# Revit family: FA_Молниеприемник_EZETEK
name_source: partatom
category: Системы пожарной сигнализации
revit_build: Autodesk Revit 2017 (Build: 20170118_1100(x64)
units: mm (PartAtom-declared; Revit-internal decimal feet)

## family parameters
Всегда вертикально = Да
На основе рабочей плоскости = Нет
Общий = Нет
При загрузке вырезать с полостями = Нет
Размер круглого соединителя = Использовать радиус
Сохранять ориентацию аннотаций = Нет
Тип детали = Нормальный
Точка расчета площади = Нет

## types (17) — shared parameters
ADSK_Версия Revit = 2017
ADSK_Единица измерения = шт.
ADSK_Завод-изготовитель = Ezetek
ADSK_Количество = 1
URL = https://ezetek.ru
Группа модели = Молниеотводы и мачты на утяжелителях
Изготовитель = Ezetek
Описание = Молниеприемник

## per-type parameters (varying)
| type | ADSK_Код изделия | ADSK_Марка | ADSK_Масса | ADSK_Масса_Текст | ADSK_Материал | ADSK_Наименование | ADSK_Обозначение | ADSK_Размер_Диаметр | ADSK_Размер_Длина |
| Молниеприемник_1м_алюм_90870 | 90870 | 90870 | 0.6 | 0.6 | BIMLIB_Алюминий_EZETEK | Молниеприемник 1 м, алюм. | 90870 | 16 мм | 1000 мм |
| Молниеприемник_0.5м_алюм_90874-2 | 90874-2 | 90874-2 | 0.3 | 0.3 | BIMLIB_Алюминий_EZETEK | Молниеприемник 0.5 м, алюм. | 90874-2 | 16 мм | 500 мм |
| Молниеприемник_0,5м_алюм_76514 | 76514 | 76514 | 0.3 | 0.3 | BIMLIB_Алюминий_EZETEK | Молниеприемник 20 мм х 0.5 м, алюм. | 76514 | 20 мм | 500 мм |
| Молниеприемник_1м_нерж_90859 | 90859 | 90859 | 1.5 | 1.5 | BIMLIB_Сталь_Нержавеющая_EZETEK | Молниеприемник 1 м, нерж. | 90859 | 16 мм | 1000 мм |
| Молниеприемник_1.5м_алюм_90871 | 90871 | 90871 | 0.9 | 0.9 | BIMLIB_Алюминий_EZETEK | Молниеприемник 1.5 м, алюм. | 90871 | 16 мм | 1500 мм |
| Молниеприемник_0.5м_нерж_90370-1 | 90370-1 | 90370-1 | 0.75 | 0.75 | BIMLIB_Сталь_Нержавеющая_EZETEK | Молниеприемник 0.5 м, нерж. | 90370-1 | 16 мм | 500 мм |
| Молниеприемник_1.5м_нерж_90370 | 90370 | 90370 | 2.25 | 2.25 | BIMLIB_Сталь_Нержавеющая_EZETEK | Молниеприемник 1.5 м, нерж. | 90370 | 16 мм | 1500 мм |
| Молниеприемник_2м_алюм_90872 | 90872 | 90872 | 1.2 | 1.2 | BIMLIB_Алюминий_EZETEK | Молниеприемник 2 м, алюм. | 90872 | 16 мм | 2000 мм |
| Молниеприемник_2м_нерж_90371 | 90371 | 90371 | 3 | 3 | BIMLIB_Сталь_Нержавеющая_EZETEK | Молниеприемник 2 м, нерж. | 90371 | 16 мм | 2000 мм |
| Молниеприемник_2.5м_алюм_90874 | 90874 | 90874 | 1.4 | 1.4 | BIMLIB_Алюминий_EZETEK | Молниеприемник 2.5 м, алюм. | 90874 | 16 мм | 2500 мм |
| Молниеприемник_3м_алюм_23404 | 23404 | 23404 | 1.8 | 1.8 | BIMLIB_Алюминий_EZETEK | Молниеприемник 20 мм х 3 м, алюм. | 23404 | 20 мм | 3000 мм |
| Молниеприемник_3м_нерж_90858 | 90858 | 90858 | 4.5 | 4.5 | BIMLIB_Сталь_Нержавеющая_EZETEK | Молниеприемник 3 м, нерж. | 90858 | 16 мм | 3000 мм |
| Молниеприемник_4м_нерж_90372 | 90372 | 90372 | 6 | 6 | BIMLIB_Сталь_Нержавеющая_EZETEK | Молниеприемник 4 м, нерж. | 90372 | 16 мм | 4000 мм |
| Молниеприемник_1м_медь_90872-4 | 90872-4 | 90872-4 | 1.8 | 1.8 | BIMLIB_Медь_EZETEK | Молниеприемник 1 м, медь | 90872-4 | 16 мм | 1000 мм |
| Молниеприемник_1.5м_медь_90872-3 | 90872-3 | 90872-3 | 2.7 | 2.7 | BIMLIB_Медь_EZETEK | Молниеприемник 1,5 м, медь | 90872-3 | 16 мм | 1500 мм |
| Молниеприемник_2м_медь_90872-1 | 90872-1 | 90872-1 | 3.6 | 3.6 | BIMLIB_Медь_EZETEK | Молниеприемник 2 м, медь | 90872-1 | 16 мм | 2000 мм |
| Молниеприемник_3м_медь_90872-2 | 90872-2 | 90872-2 | 5.4 | 5.4 | BIMLIB_Медь_EZETEK | Молниеприемник 3 м, медь | 90872-2 | 16 мм | 3000 мм |
